# Revit family: Thorn Caelon S7i
name_source: partatom
category: Lighting Fixtures
units: mm (PartAtom-declared; Revit-internal decimal feet)

## family parameters
Cut with Voids When Loaded = No
Host = Face
Light Source = No
Maintain Annotation Orientation = No
Part Type = Normal
Room Calculation Point = No
Round Connector Dimension = Use Diameter
Shared = No

## types (24) — shared parameters
Apparent Load = 20 VA
Assembly Code = Pr_70_70_48_75
Description = Outdoor flood and spotlight luminaires
Export Type to IFC As = IfcLightFixtureType
Lamp = LED
Luminaire Height = 127.02 mm  [stored 0.416732 ft]
Luminaire Length = 107.5 mm
Luminaire Width = 86 mm  [stored 0.282152 ft]
Manufacturer = Thorn Lighting
Power Factor = 1
Type Bracket Black = Thorn-Parts-CAELON-Bracket-S7x : Black
Type Bracket White = Thorn-Parts-CAELON-Bracket-S7x : White
Type Housing Black = Thorn-Parts-CAELON-Housing-S7i : Black
Type Housing White = Thorn-Parts-CAELON-Housing-S7i : White
Type IFC Predefined Type = DIRECTIONSOURCE
URL = https://www.thornlighting.com
Wattage = 11 VA
zero-valued in all types: Default Elevation

## per-type parameters (varying)
| type | Housing Finish Black | Housing Finish White | Model | Optic | Type Bracket | Type Housing | Type Image | Type Light Source |
| CAELON S7I 700-827 F BK 66 HF | Yes | No | 21035848 | Far | Thorn-Parts-CAELON-Bracket-S7x : Black | Thorn-Parts-CAELON-Housing-S7i : Black | TLG_CAEL_F_S7i_BK.jpg | Thorn-Light Sources-CAELON S7i : CAELON S7I 700-827 F BK 66 HF_photometric_data |
| CAELON S7I 700-827 F WH 66 HF | No | Yes | 21035849 | Far | Thorn-Parts-CAELON-Bracket-S7x : White | Thorn-Parts-CAELON-Housing-S7i : White | TLG_CAEL_F_S7i_WH.jpg | Thorn-Light Sources-CAELON S7i : CAELON S7I 700-827 F WH 66 HF_photometric_data |
| CAELON S7I 700-827 M BK 66 HF | Yes | No | 21035846 | Medium | Thorn-Parts-CAELON-Bracket-S7x : Black | Thorn-Parts-CAELON-Housing-S7i : Black | TLG_CAEL_F_S7i_BK.jpg | Thorn-Light Sources-CAELON S7i : CAELON S7I 700-827 M BK 66 HF_photometric_data |
| CAELON S7I 700-827 M WH 66 HF | No | Yes | 21035847 | Medium | Thorn-Parts-CAELON-Bracket-S7x : White | Thorn-Parts-CAELON-Housing-S7i : White | TLG_CAEL_F_S7i_WH.jpg | Thorn-Light Sources-CAELON S7i : CAELON S7I 700-827 M WH 66 HF_photometric_data |
| CAELON S7I 700-827 N BK 66 HF | Yes | No | 21035844 | Narrow | Thorn-Parts-CAELON-Bracket-S7x : Black | Thorn-Parts-CAELON-Housing-S7i : Black | TLG_CAEL_F_S7i_BK.jpg | Thorn-Light Sources-CAELON S7i : CAELON S7I 700-827 N BK 66 HF_photometric_data |
| CAELON S7I 700-827 N WH 66 HF | No | Yes | 21035845 | Narrow | Thorn-Parts-CAELON-Bracket-S7x : White | Thorn-Parts-CAELON-Housing-S7i : White | TLG_CAEL_F_S7i_WH.jpg | Thorn-Light Sources-CAELON S7i : CAELON S7I 700-827 N WH 66 HF_photometric_data |
| CAELON S7I 700-827 SN BK 66 HF | Yes | No | 21035842 | Super Narrow | Thorn-Parts-CAELON-Bracket-S7x : Black | Thorn-Parts-CAELON-Housing-S7i : Black | TLG_CAEL_F_S7i_BK.jpg | Thorn-Light Sources-CAELON S7i : CAELON S7I 700-827 SN BK 66 HF_photometric_data |
| CAELON S7I 700-827 SN WH 66 HF | No | Yes | 21035843 | Super Narrow | Thorn-Parts-CAELON-Bracket-S7x : White | Thorn-Parts-CAELON-Housing-S7i : White | TLG_CAEL_F_S7i_WH.jpg | Thorn-Light Sources-CAELON S7i : CAELON S7I 700-827 SN WH 66 HF_photometric_data |
| CAELON S7I 700-830 F BK 66 HF | Yes | No | 21035856 | Far | Thorn-Parts-CAELON-Bracket-S7x : Black | Thorn-Parts-CAELON-Housing-S7i : Black | TLG_CAEL_F_S7i_BK.jpg | Thorn-Light Sources-CAELON S7i : CAELON S7I 700-830 F BK 66 HF_photometric_data |
| CAELON S7I 700-830 F WH 66 HF | No | Yes | 21035857 | Far | Thorn-Parts-CAELON-Bracket-S7x : White | Thorn-Parts-CAELON-Housing-S7i : White | TLG_CAEL_F_S7i_WH.jpg | Thorn-Light Sources-CAELON S7i : CAELON S7I 700-830 F WH 66 HF_photometric_data |
| CAELON S7I 700-830 M BK 66 HF | Yes | No | 21035854 | Medium | Thorn-Parts-CAELON-Bracket-S7x : Black | Thorn-Parts-CAELON-Housing-S7i : Black | TLG_CAEL_F_S7i_BK.jpg | Thorn-Light Sources-CAELON S7i : CAELON S7I 700-830 M BK 66 HF_photometric_data |
| CAELON S7I 700-830 M WH 66 HF | No | Yes | 21035855 | Medium | Thorn-Parts-CAELON-Bracket-S7x : White | Thorn-Parts-CAELON-Housing-S7i : White | TLG_CAEL_F_S7i_WH.jpg | Thorn-Light Sources-CAELON S7i : CAELON S7I 700-830 M WH 66 HF_photometric_data |
| CAELON S7I 700-830 N BK 66 HF | Yes | No | 21035852 | Narrow | Thorn-Parts-CAELON-Bracket-S7x : Black | Thorn-Parts-CAELON-Housing-S7i : Black | TLG_CAEL_F_S7i_BK.jpg | Thorn-Light Sources-CAELON S7i : CAELON S7I 700-830 N BK 66 HF_photometric_data |
| CAELON S7I 700-830 N WH 66 HF | No | Yes | 21035853 | Narrow | Thorn-Parts-CAELON-Bracket-S7x : White | Thorn-Parts-CAELON-Housing-S7i : White | TLG_CAEL_F_S7i_WH.jpg | Thorn-Light Sources-CAELON S7i : CAELON S7I 700-830 N WH 66 HF_photometric_data |
| CAELON S7I 700-830 SN BK 66 HF | Yes | No | 21035850 | Super Narrow | Thorn-Parts-CAELON-Bracket-S7x : Black | Thorn-Parts-CAELON-Housing-S7i : Black | TLG_CAEL_F_S7i_BK.jpg | Thorn-Light Sources-CAELON S7i : CAELON S7I 700-830 SN BK 66 HF_photometric_data |
| CAELON S7I 700-830 SN WH 66 HF | No | Yes | 21035851 | Super Narrow | Thorn-Parts-CAELON-Bracket-S7x : White | Thorn-Parts-CAELON-Housing-S7i : White | TLG_CAEL_F_S7i_WH.jpg | Thorn-Light Sources-CAELON S7i : CAELON S7I 700-830 SN WH 66 HF_photometric_data |
| CAELON S7I 700-840 F BK 66 HF | Yes | No | 21035864 | Far | Thorn-Parts-CAELON-Bracket-S7x : Black | Thorn-Parts-CAELON-Housing-S7i : Black | TLG_CAEL_F_S7i_BK.jpg | Thorn-Light Sources-CAELON S7i : CAELON S7I 700-840 F BK 66 HF_photometric_data |
| CAELON S7I 700-840 F WH 66 HF | No | Yes | 21035865 | Far | Thorn-Parts-CAELON-Bracket-S7x : White | Thorn-Parts-CAELON-Housing-S7i : White | TLG_CAEL_F_S7i_WH.jpg | Thorn-Light Sources-CAELON S7i : CAELON S7I 700-840 F WH 66 HF_photometric_data |
| CAELON S7I 700-840 M BK 66 HF | Yes | No | 21035862 | Medium | Thorn-Parts-CAELON-Bracket-S7x : Black | Thorn-Parts-CAELON-Housing-S7i : Black | TLG_CAEL_F_S7i_BK.jpg | Thorn-Light Sources-CAELON S7i : CAELON S7I 700-840 M BK 66 HF_photometric_data |
| CAELON S7I 700-840 M WH 66 HF | No | Yes | 21035863 | Medium | Thorn-Parts-CAELON-Bracket-S7x : White | Thorn-Parts-CAELON-Housing-S7i : White | TLG_CAEL_F_S7i_WH.jpg | Thorn-Light Sources-CAELON S7i : CAELON S7I 700-840 M WH 66 HF_photometric_data |
| CAELON S7I 700-840 N BK 66 HF | Yes | No | 21035860 | Narrow | Thorn-Parts-CAELON-Bracket-S7x : Black | Thorn-Parts-CAELON-Housing-S7i : Black | TLG_CAEL_F_S7i_BK.jpg | Thorn-Light Sources-CAELON S7i : CAELON S7I 700-840 N BK 66 HF_photometric_data |
| CAELON S7I 700-840 N WH 66 HF | No | Yes | 21035861 | Narrow | Thorn-Parts-CAELON-Bracket-S7x : White | Thorn-Parts-CAELON-Housing-S7i : White | TLG_CAEL_F_S7i_WH.jpg | Thorn-Light Sources-CAELON S7i : CAELON S7I 700-840 N WH 66 HF_photometric_data |
| CAELON S7I 700-840 SN BK 66 HF | Yes | No | 21035858 | Super Narrow | Thorn-Parts-CAELON-Bracket-S7x : Black | Thorn-Parts-CAELON-Housing-S7i : Black | TLG_CAEL_F_S7i_BK.jpg | Thorn-Light Sources-CAELON S7i : CAELON S7I 700-840 SN BK 66 HF_photometric_data |
| CAELON S7I 700-840 SN WH 66 HF | No | Yes | 21035859 | Super Narrow | Thorn-Parts-CAELON-Bracket-S7x : White | Thorn-Parts-CAELON-Housing-S7i : White | TLG_CAEL_F_S7i_WH.jpg | Thorn-Light Sources-CAELON S7i : CAELON S7I 700-840 SN WH 66 HF_photometric_data |

note: [stored X ft] marks values corroborated as IEEE doubles in the binary element streams (Revit-internal decimal feet)

## geometry (parser evidence)
native form markers: Sweep x10
no freeform markers — native parametric forms only
